# Revit family: 6767d71d_bfa3_4480_b376_f025c8c810d8
name_source: partatom
category: Generic Models
revit_build: Autodesk Revit Architecture 2015 (Build: 20140606_1530(x64)
units: mm (PartAtom-declared; Revit-internal decimal feet)

## types (1)
- Default
    BIMobject category = Urinals
    BOSUseNativeGeometries = 0
    Brand url = http://www.duravit.com
    Date of publishing = 1/11/2017
    Edition number = 1
    IFC Classification = Sanitary Terminal
    Installation instructions = http://pro.duravit.com
    Manufacturer name = DURAVIT
    Masterformat 2014 Code = 22 41 13.16
    Masterformat 2014 Description = Residential Urinals
    NBS Reference Code = 31-93
    NBS Reference Description = Urinal And Wc Fittings
    Nominal height = 0
    Nominal width = 355
    OmniClass Code = 23-31 21 00
    OmniClass Description = Urinals
    Product Guid = 04b0511e-f2a7-48be-8289-f6f9769f3d90
    Product SKU = me-by-starck-urinal-me-by-starck-dry-281430
    Product certification = http://pro.duravit.com
    Product data url = https://bimobject.com
    Product family = ME by Starck
    Product group = Urinal ME by Starck Dry
    Product name = ME by Starck Urinal ME by Starck Dry 281430
    Product url = http://pro.duravit.com
    QR code = http://bimobject.com
    Technical description = http://pro.duravit.com
    UNSPSC Code = 30181506
    Uniclass 1.4 Code = L721
    Uniclass 1.4 Description = Sanitary equipment
    Uniclass 2.0 Code = PR-31-93
    Uniclass 2.0 Description = Urinal And Wc Fittings
    Uniclass 2015 Code = Pr_40_20_93
    Uniclass 2015 Name = Urinal and WC fittings
    Uniformat II Code = D2010
    Uniformat II Description = Plumbing Fixtures
    Weight Net (Kg) = 14.2

## geometry (parser evidence)
native form markers: Sweep x2
no freeform markers — native parametric forms only
